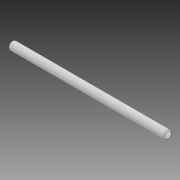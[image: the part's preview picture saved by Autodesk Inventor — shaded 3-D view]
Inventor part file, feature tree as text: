
AUTODESK INVENTOR PART (.ipt)
format: ipt  version: 2020 (Build 240168000, 168)  size: 79,360 bytes
history: native  units: mm
features: revolve x1, sketch x1
ambient origin geometry x8: Origin, YZ Plane, XZ Plane, XY Plane, X Axis, Y Axis, Z Axis, Center Point
bodies: Solid1 (feature_tree)
feature tree (2):
  revolve  "Revolution1"  Angle=135.0deg
  sketch  "Sketch1"  dims[d0=4.0mm d1=135.0deg d2=1.0mm d3=160.0mm d4=90.0deg]
